# Revit family: Tuffo 1700 Built In Bath (No Handle) - White
name_source: partatom
category: Plumbing Fixtures
units: mm (PartAtom-declared; Revit-internal decimal feet)

## family parameters
Always vertical = Yes
Cut with Voids When Loaded = No
Enable Cutting in Views = No
Maintain Annotation Orientation = No
OmniClass Number = 23.45.00.00
OmniClass Title = Sanitary, Laundry, and Cleaning Equipment
Part Type = Normal
Room Calculation Point = No
Round Connector Dimension = Use Diameter
Shared = No
Work Plane-Based = No

## types (1)
- Tuffo 1700 Built In Bath (No Handle) - White
    Bath Finish = White Acrylic
    Category = Baths
    Colour = White
    Default Elevation = 0 mm  [stored 0 ft]
    Height = 440 mm  [stored 1.44357 ft]
    Length = 1700 mm  [stored 5.57743 ft]
    Manufacturer = Lecico SA
    Material = Sanitary Grade Acrylic
    Model = Tuffo 1700 Built In Bath (No Handle) - White
    Product Code = BATTUFFO00000US
    Technical Dimensions = W1700 x H440 x D700mm
    URL = https://www.lecicosa.co.za
    Waste = Aluminium
    Width = 700 mm  [stored 2.29659 ft]

note: [stored X ft] marks values corroborated as IEEE doubles in the binary element streams (Revit-internal decimal feet)

## geometry (parser evidence)
native form markers: Blend x2, Sweep x2
no freeform markers — native parametric forms only
